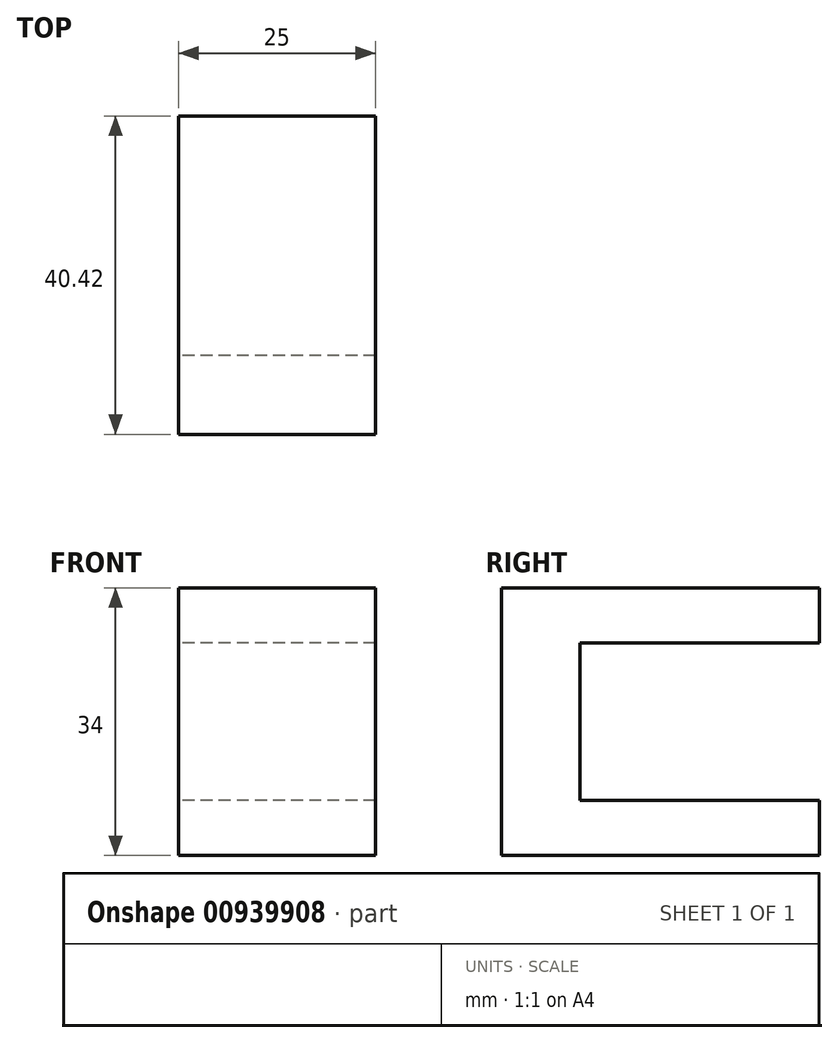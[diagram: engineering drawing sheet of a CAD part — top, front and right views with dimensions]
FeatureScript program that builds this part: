
annotation { "Feature Type Name" : "Feature", "Feature Type Description" : "" }
export const myFeature = defineFeature(function(context is Context, id is Id, definition is map)
    precondition{}
    {
        {
            var Q0;
            Q0=qCreatedBy(makeId("Right.planeOp"),FACE);
            var sketch = newSketch(context, id + "F0", { "sketchPlane" : qUnion([Q0])});
            skLineSegment(sketch, "E0", {"start": v(0, 10) * mm, "end": v(0, -10) * mm});
            skLineSegment(sketch, "E1", {"start": v(0, 10) * mm, "end": v(30.42, 10) * mm});
            skLineSegment(sketch, "E2", {"start": v(30.42, 10) * mm, "end": v(30.42, 17) * mm});
            skLineSegment(sketch, "E3", {"start": v(30.42, 17) * mm, "end": v(-10, 17) * mm});
            skLineSegment(sketch, "E4", {"start": v(-10, 17) * mm, "end": v(-10, -17) * mm});
            skLineSegment(sketch, "E5", {"start": v(-10, -17) * mm, "end": v(30.42, -17) * mm});
            skLineSegment(sketch, "E6", {"start": v(30.42, -17) * mm, "end": v(30.42, -10) * mm});
            skLineSegment(sketch, "E7", {"start": v(30.42, -10) * mm, "end": v(0, -10) * mm});
            skSolve(sketch);
        }
        {
            var Q0;
            Q0=makeQuery(id+"F0.imprint","IMPRINT",FACE,{"disambiguationData":[TD([[makeQuery(id+"F0.imprint","IMPRINT",EDGE,{"derivedFrom":sQuery(id+"F0.wireOp",EDGE,"E0")}),-1.0]])]});
            extrude(context, id + "F1", {"entities" : qUnion([Q0]), "depth" : 25 * mm, "offsetDistance" : 25 * mm});
        }
    });
